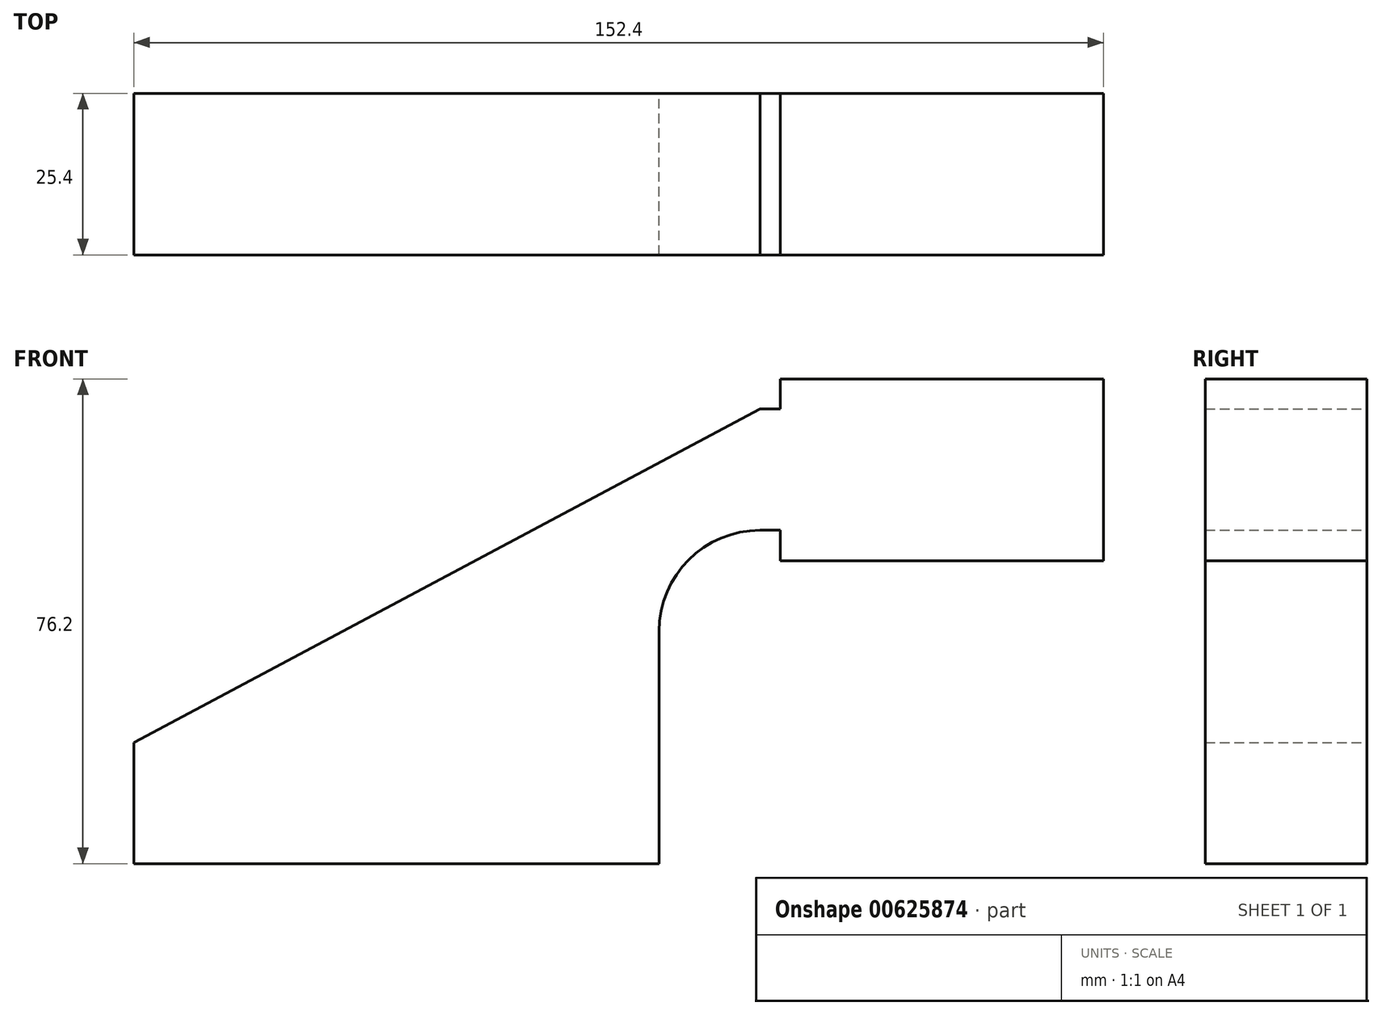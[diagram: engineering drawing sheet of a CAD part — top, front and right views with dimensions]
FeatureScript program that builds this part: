
annotation { "Feature Type Name" : "Feature", "Feature Type Description" : "" }
export const myFeature = defineFeature(function(context is Context, id is Id, definition is map)
    precondition{}
    {
        {
            var Q0;
            Q0=qCreatedBy(makeId("Front.planeOp"),FACE);
            var sketch = newSketch(context, id + "F0", { "sketchPlane" : qUnion([Q0])});
            skLineSegment(sketch, "E0.bottom", {"start": v(41.28, -9.52) * mm, "end": v(-41.28, -9.52) * mm});
            skLineSegment(sketch, "E0.top", {"start": v(41.28, 9.53) * mm, "end": v(-41.28, 9.53) * mm});
            skLineSegment(sketch, "E0.left", {"start": v(41.28, -9.52) * mm, "end": v(41.28, 9.53) * mm});
            skLineSegment(sketch, "E0.right", {"start": v(-41.28, -9.52) * mm, "end": v(-41.28, 9.53) * mm});
            skPoint(sketch, "E0.middle", {"position": v(0, 0) * mm});
            skLineSegment(sketch, "E1.bottom", {"start": v(111.12, 38.1) * mm, "end": v(60.32, 38.1) * mm});
            skLineSegment(sketch, "E1.top", {"start": v(111.12, 66.67) * mm, "end": v(60.32, 66.67) * mm});
            skLineSegment(sketch, "E1.left", {"start": v(111.12, 38.1) * mm, "end": v(111.12, 66.68) * mm});
            skLineSegment(sketch, "E1.right", {"start": v(60.32, 38.1) * mm, "end": v(60.32, 66.68) * mm});
            skPoint(sketch, "E1.middle", {"position": v(85.72, 52.39) * mm});
            skLineSegment(sketch, "E2", {"start": v(41.28, 9.53) * mm, "end": v(41.28, 27) * mm});
            skArc(sketch, "E3", {"start": v(41.28, 27) * mm, "mid": v(45.92, 38.23) * mm, "end": v(57.15, 42.88) * mm});
            skLineSegment(sketch, "E4", {"start": v(57.15, 42.88) * mm, "end": v(85.56, 42.88) * mm});
            skLineSegment(sketch, "E5.0", {"start": v(57.15, 61.93) * mm, "end": v(81.15, 61.93) * mm});
            skArc(sketch, "E5.1", {"start": v(22.23, 27) * mm, "mid": v(32.45, 51.7) * mm, "end": v(57.15, 61.93) * mm});
            skLineSegment(sketch, "E5.2", {"start": v(22.23, 9.53) * mm, "end": v(22.23, 27) * mm});
            skFitSpline(sketch, "E6", {"points": [v(57.15, 61.93) * mm, v(-41.28, 9.53) * mm], "startDerivative": vector(-98.43, -52.4) * mm, "endDerivative": vector(-98.43, -52.4) * mm});
            skSolve(sketch);
        }
        {
            var Q0;
            {var subQ1=sQuery(id+"F0.wireOp",EDGE,"E1.bottom");Q0=makeQuery(id+"F0.imprint","IMPRINT",FACE,{"disambiguationData":[TD([[makeQuery(id+"F0.imprint","IMPRINT",EDGE,{"derivedFrom":subQ1}),-1.0]])]});}
            var Q1;
            {var subQ0=sQuery(id+"F0.wireOp",EDGE,"84606f76-c037-45eb-8129-abd2f34198b4");var subQ1=sQuery(id+"F0.wireOp",EDGE,"E5.1");var subQ3=makeQuery(id+"F0.imprint","INTERSECT",VERTEX,{"derivedFrom":[subQ1,subQ0]});Q1=makeQuery(id+"F0.imprint","IMPRINT",FACE,{"disambiguationData":[TD([[makeQuery(id+"F0.imprint","IMPRINT",EDGE,{"disambiguationData":[TD([[subQ3,-1.0]])],"derivedFrom":subQ1}),-1.0]])]});}
            var Q2;
            Q2=makeQuery(id+"F0.imprint","IMPRINT",FACE,{"disambiguationData":[TD([[makeQuery(id+"F0.imprint","IMPRINT",EDGE,{"derivedFrom":sQuery(id+"F0.wireOp",EDGE,"E0.bottom")}),-1.0]])]});
            var Q3;
            {var subQ1=sQuery(id+"F0.wireOp",EDGE,"E2");Q3=makeQuery(id+"F0.imprint","IMPRINT",FACE,{"disambiguationData":[TD([[makeQuery(id+"F0.imprint","IMPRINT",EDGE,{"derivedFrom":subQ1}),1.0]])]});}
            var Q4;
            {var subQ3=sQuery(id+"F0.wireOp",EDGE,"E5.2");Q4=makeQuery(id+"F0.imprint","IMPRINT",FACE,{"disambiguationData":[TD([[makeQuery(id+"F0.imprint","IMPRINT",EDGE,{"derivedFrom":subQ3}),1.0]])]});}
            extrude(context, id + "F1", {"entities" : qUnion([Q0, Q1, Q2, Q3, Q4]), "depth" : 25.4 * mm, "offsetDistance" : 25.4 * mm});
        }
    });
